# Revit family: 63_UN_LF_SM_Code MEN12
name_source: partatom
category: Lighting Fixtures
units: mm (PartAtom-declared; Revit-internal decimal feet)

## family parameters
Always vertical = Yes
Cut with Voids When Loaded = Yes
Light Source = No
OmniClass Number = 23.80.70.11.14
OmniClass Title = General Luminaries, Directional
Part Type = Normal
Room Calculation Point = Yes
Round Connector Dimension = Use Diameter
Shared = No
Work Plane-Based = No

## types (6) — shared parameters
Assembly Code = 63.0
Housing_Material = Plastic, Opaque Black
IfcExportAs = IfcLightFixtureType
IfcExportType = USERDEFINED
Lamp = LED
Manufacturer = Light International
URL = https://lightinternational.nl
Voltage = 230 V

## per-type parameters (varying)
| type | Apparent Load | Light Source | Lightsource_tilt | Luminous Flux (lm) | Model | Type Comments | Wattage Comments |
| MEN122 - Wall mounted | 18 VA | MEN12 Geometry : MEN122 | 90.00° | 2500 lm | MEN122 | MEN122 | 17.6W |
| MEN122 - Ceiling mounted | 18 VA | MEN12 Geometry : MEN122 | 180.00° | 2500 lm | MEN122 | MEN122 | 17.6W |
| MEN123 - Ceiling mounted | 24 VA | MEN12 Geometry : MEN123 | 180.00° | 3300 lm | MEN123 | MEN123 | 23.8W |
| MEN123 - Wall mounted | 24 VA | MEN12 Geometry : MEN123 | 90.00° | 3300 lm | MEN123 | MEN123 | 23.8W |
| MEN124 - Wall mounted | 32 VA | MEN12 Geometry : MEN124 | 90.00° | 4400 lm | MEN124 | MEN124 | 31.5W |
| MEN124 - Ceiling mounted | 32 VA | MEN12 Geometry : MEN124 | 180.00° | 4400 lm | MEN124 | MEN124 | 31.5W |

## geometry (parser evidence)
native form markers: Sweep x16
no freeform markers — native parametric forms only
